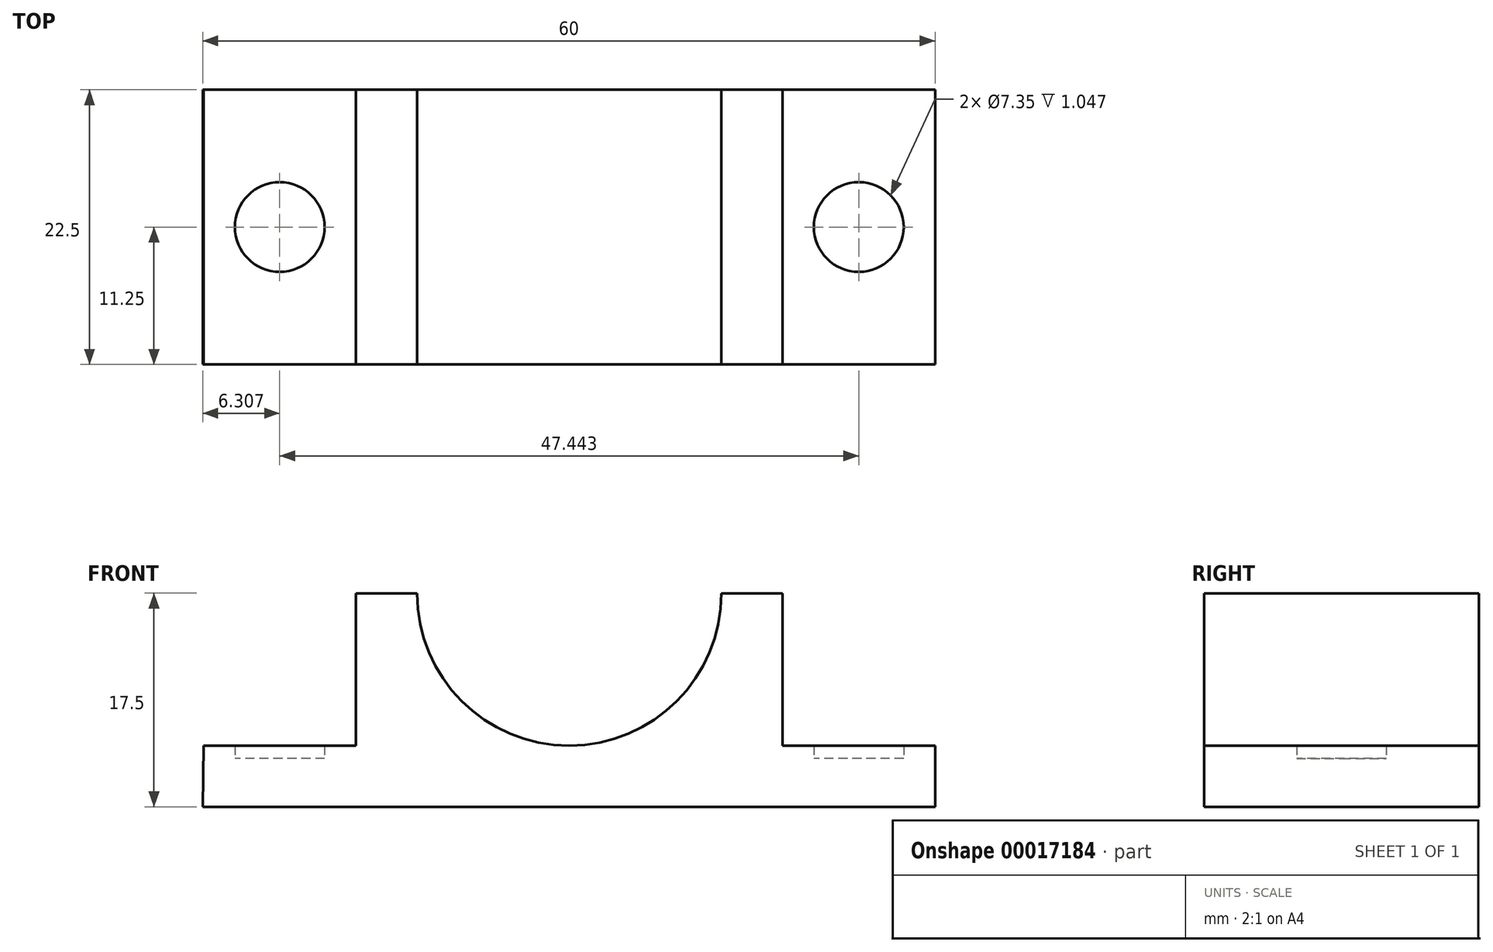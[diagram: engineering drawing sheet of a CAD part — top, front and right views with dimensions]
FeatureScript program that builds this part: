
annotation { "Feature Type Name" : "Feature", "Feature Type Description" : "" }
export const myFeature = defineFeature(function(context is Context, id is Id, definition is map)
    precondition{}
    {
        {
            var Q0;
            Q0=qCreatedBy(makeId("Front.planeOp"),FACE);
            var sketch = newSketch(context, id + "F0", { "sketchPlane" : qUnion([Q0])});
            skLineSegment(sketch, "E0", {"start": v(-36.05, 1.05) * mm, "end": v(-23.55, 1.05) * mm});
            skLineSegment(sketch, "E1", {"start": v(-23.55, 1.05) * mm, "end": v(-23.55, 13.55) * mm});
            skLineSegment(sketch, "E2", {"start": v(-23.55, 13.55) * mm, "end": v(-18.55, 13.55) * mm});
            skLineSegment(sketch, "E3", {"start": v(-18.55, 13.55) * mm, "end": v(-18.55, 13.55) * mm});
            skLineSegment(sketch, "E4", {"start": v(-6.1, 1.05) * mm, "end": v(-6.05, 1.05) * mm});
            skLineSegment(sketch, "E5", {"start": v(6.4, 13.55) * mm, "end": v(6.4, 13.55) * mm});
            skLineSegment(sketch, "E6", {"start": v(6.4, 13.55) * mm, "end": v(11.4, 13.55) * mm});
            skLineSegment(sketch, "E7", {"start": v(11.4, 13.55) * mm, "end": v(11.4, 1.05) * mm});
            skLineSegment(sketch, "E8", {"start": v(11.4, 1.05) * mm, "end": v(23.9, 1.05) * mm});
            skLineSegment(sketch, "E9", {"start": v(23.9, 1.05) * mm, "end": v(23.9, -3.95) * mm});
            skLineSegment(sketch, "E10", {"start": v(23.9, -3.95) * mm, "end": v(-36.1, -3.95) * mm});
            skLineSegment(sketch, "E11", {"start": v(-36.1, -3.95) * mm, "end": v(-36.05, 1.05) * mm});
            skPoint(sketch, "E12.visualSharp", {"position": v(-18.55, 1.05) * mm});
            skArc(sketch, "E12.filletArc", {"start": v(-18.55, 13.55) * mm, "mid": v(-14.9, 4.7) * mm, "end": v(-6.05, 1.05) * mm});
            skPoint(sketch, "E13.visualSharp", {"position": v(6.4, 1.05) * mm});
            skArc(sketch, "E13.filletArc", {"start": v(-6.1, 1.05) * mm, "mid": v(2.73, 4.7) * mm, "end": v(6.4, 13.55) * mm});
            skSolve(sketch);
        }
        {
            var Q0;
            Q0 = qSketchRegion(id + "F0", true);
            extrude(context, id + "F1", {"entities" : qUnion([Q0]), "depth" : 22.5 * mm});
        }
        {
            var Q0;
            Q0=qCreatedBy(makeId("Top.planeOp"),FACE);
            var sketch = newSketch(context, id + "F2", { "sketchPlane" : qUnion([Q0])});
            skCircle(sketch, "E14", {"center": v(17.64, -11.25) * mm, "radius": 3.68 * mm});
            skCircle(sketch, "E15", {"center": v(-29.8, -11.25) * mm, "radius": 3.68 * mm});
            skSolve(sketch);
        }
        {
            var Q0;
            Q0 = qSketchRegion(id + "F2", true);
            extrude(context, id + "F3", {"entities" : qUnion([Q0]), "operationType" : NewBodyOperationType.REMOVE, "depth" : 38.2 * mm});
        }
    });
